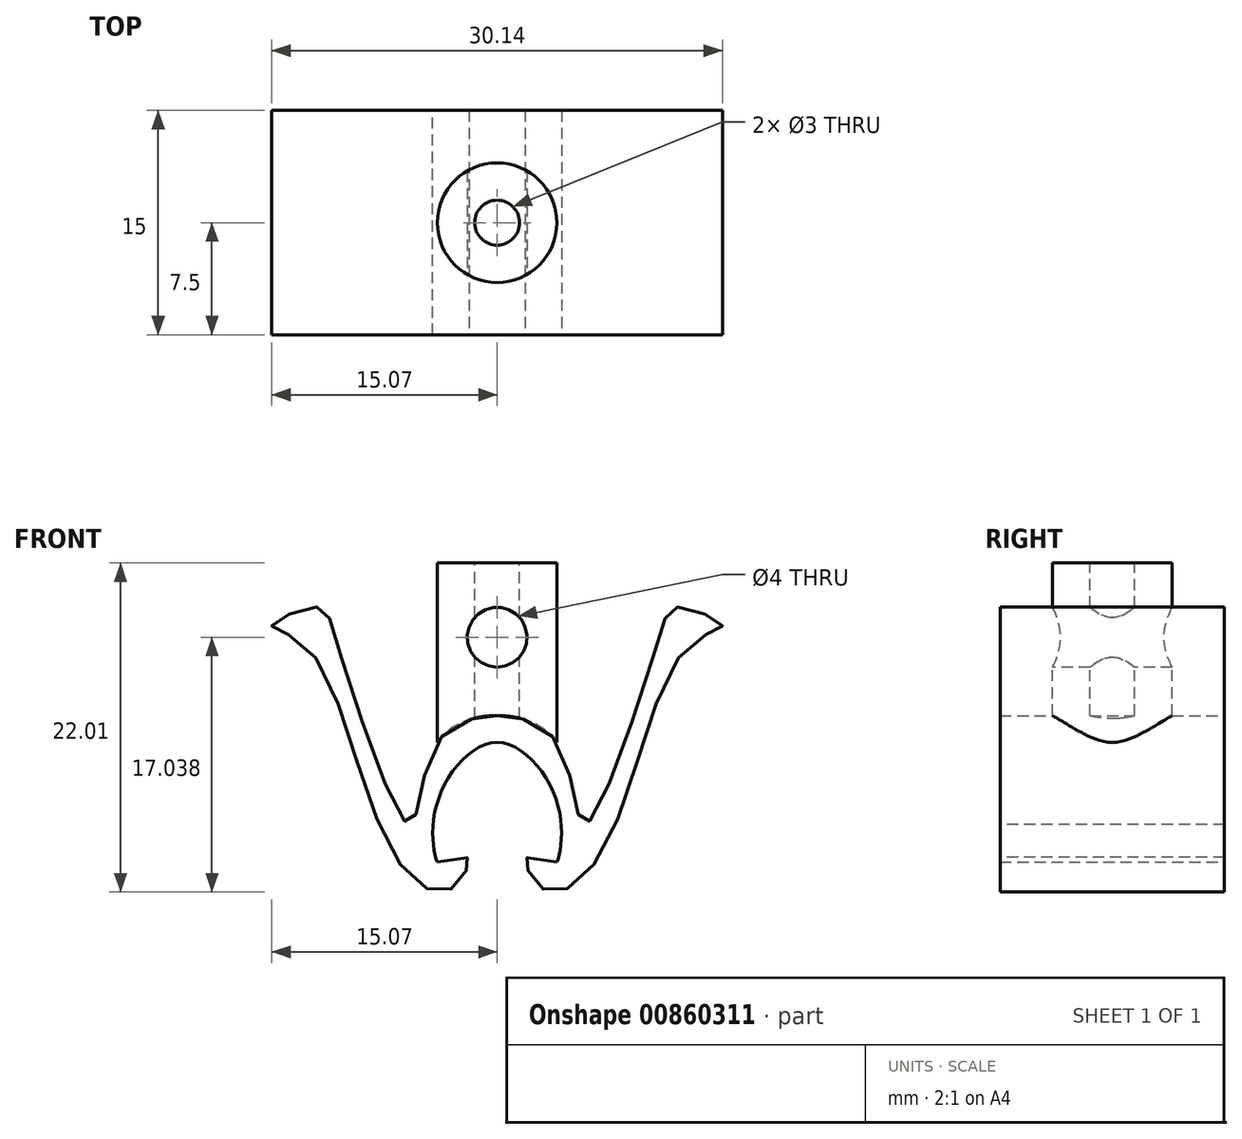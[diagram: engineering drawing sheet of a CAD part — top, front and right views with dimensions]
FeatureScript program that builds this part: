
annotation { "Feature Type Name" : "Feature", "Feature Type Description" : "" }
export const myFeature = defineFeature(function(context is Context, id is Id, definition is map)
    precondition{}
    {
        {
            var Q0;
            Q0=qCreatedBy(makeId("Front.planeOp"),FACE);
            var sketch = newSketch(context, id + "F0", { "sketchPlane" : qUnion([Q0])});
            skLineSegment(sketch, "E0.bottom", {"start": v(-4, 0) * mm, "end": v(4, 0) * mm, "construction": true});
            skLineSegment(sketch, "E0.top", {"start": v(-4, 8) * mm, "end": v(4, 8) * mm, "construction": true});
            skLineSegment(sketch, "E0.left", {"start": v(-4, 0) * mm, "end": v(-4, 8) * mm, "construction": true});
            skLineSegment(sketch, "E0.right", {"start": v(4, 0) * mm, "end": v(4, 8) * mm, "construction": true});
            skPoint(sketch, "E1", {"position": v(-4, 4) * mm});
            skFitSpline(sketch, "E2", {"points": [v(-4, 0) * mm, v(-4, 4) * mm, v(0, 8) * mm], "startDerivative": vector(-1.93, 4.62) * mm, "endDerivative": vector(9.5, 0) * mm});
            skFitSpline(sketch, "E3.MirrorCS", {"points": [v(4, 0) * mm, v(4, 4) * mm, v(0, 8) * mm], "startDerivative": vector(1.93, 4.62) * mm, "endDerivative": vector(-9.5, 0) * mm});
            skFitSpline(sketch, "E4.MirrorCS", {"points": [v(4, 0) * mm, v(1.88, 0) * mm, v(3.22, -1.9) * mm, v(7.12, 0.84) * mm, v(12.8, 14.45) * mm, v(15.06, 15.85) * mm, v(12.17, 17.05) * mm, v(10.93, 15.35) * mm, v(5.89, 2.52) * mm, v(4, 8) * mm, v(0, 9.79) * mm], "startDerivative": vector(-83.4, 18.85) * mm, "endDerivative": vector(-27.27, 0) * mm});
            skFitSpline(sketch, "E5.MirrorCS", {"points": [v(-4, 0) * mm, v(-1.88, 0) * mm, v(-3.22, -1.9) * mm, v(-7.12, 0.84) * mm, v(-12.8, 14.45) * mm, v(-15.06, 15.85) * mm, v(-12.17, 17.05) * mm, v(-10.93, 15.35) * mm, v(-5.89, 2.52) * mm, v(-4, 8) * mm, v(0, 9.79) * mm], "startDerivative": vector(83.4, 18.85) * mm, "endDerivative": vector(27.27, 0) * mm});
            skSolve(sketch);
        }
        {
            var Q0;
            Q0=makeQuery(id+"F0.imprint","IMPRINT",FACE,{"disambiguationData":[TD([[makeQuery(id+"F0.imprint","IMPRINT",EDGE,{"derivedFrom":sQuery(id+"F0.wireOp",EDGE,"E2")}),1.0]])]});
            extrude(context, id + "F1", {"entities" : qUnion([Q0]), "endBound" : BoundingType.SYMMETRIC, "depth" : 15 * mm, "offsetDistance" : 25 * mm});
        }
        {
            var Q0;
            Q0=qCreatedBy(makeId("Top.planeOp"),FACE);
            cPlane(context, id + "F2", {"entities" : qUnion([Q0]), "cplaneType" : CPlaneType.OFFSET, "offset" : 20 * mm, "width" : 150 * mm, "height" : 150 * mm});
        }
        {
            var Q0;
            Q0=qCreatedBy(id+"F2.planeOp",FACE);
            var sketch = newSketch(context, id + "F3", { "sketchPlane" : qUnion([Q0])});
            skCircle(sketch, "E6", {"center": v(0, 0) * mm, "radius": 1.5 * mm});
            skCircle(sketch, "E7", {"center": v(0, 0) * mm, "radius": 4 * mm});
            skSolve(sketch);
        }
        {
            var Q0;
            Q0=makeQuery(id+"F3.imprint","IMPRINT",FACE,{"disambiguationData":[TD([[makeQuery(id+"F3.imprint","IMPRINT",EDGE,{"derivedFrom":sQuery(id+"F3.wireOp",EDGE,"E6")}),-1.0]])]});
            extrude(context, id + "F4", {"entities" : qUnion([Q0]), "operationType" : NewBodyOperationType.ADD, "endBound" : BoundingType.UP_TO_NEXT, "oppositeDirection" : true, "depth" : 25 * mm, "offsetDistance" : 25 * mm});
        }
        {
            var Q0;
            Q0=qCreatedBy(makeId("Front.planeOp"),FACE);
            var sketch = newSketch(context, id + "F5", { "sketchPlane" : qUnion([Q0])});
            skCircle(sketch, "E8", {"center": v(0, 15.03) * mm, "radius": 2 * mm});
            skSolve(sketch);
        }
        {
            var Q0;
            Q0=makeQuery(id+"F5.imprint","IMPRINT",FACE,{"disambiguationData":[TD([[makeQuery(id+"F5.imprint","IMPRINT",EDGE,{"derivedFrom":sQuery(id+"F5.wireOp",EDGE,"E8")}),1.0]])]});
            extrude(context, id + "F6", {"entities" : qUnion([Q0]), "operationType" : NewBodyOperationType.REMOVE, "endBound" : BoundingType.SYMMETRIC, "oppositeDirection" : true, "depth" : 25 * mm, "offsetDistance" : 25 * mm});
        }
    });
